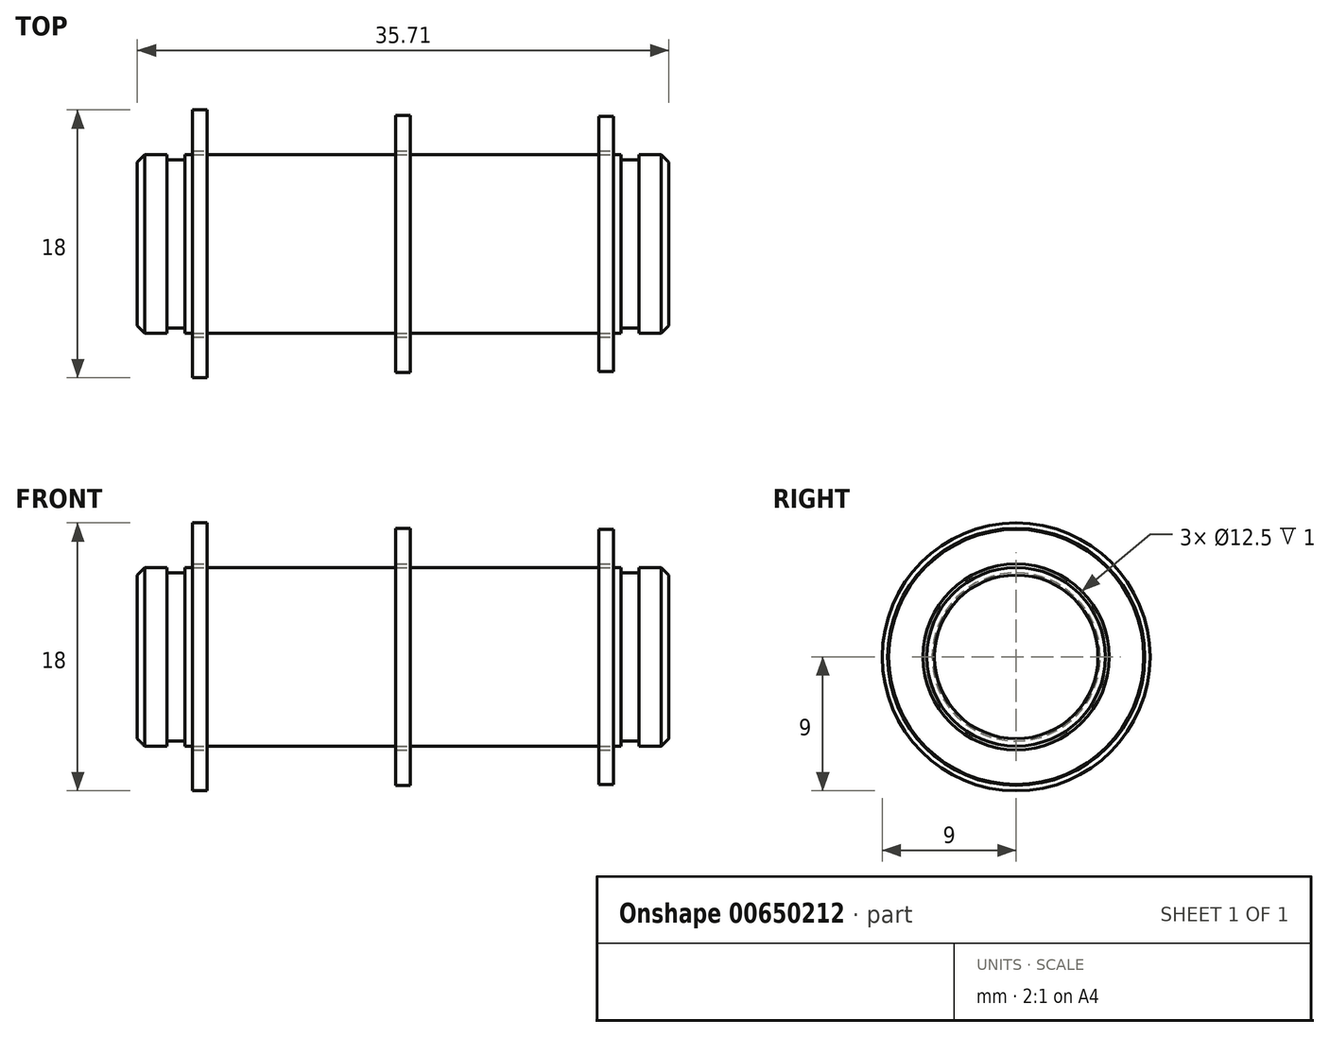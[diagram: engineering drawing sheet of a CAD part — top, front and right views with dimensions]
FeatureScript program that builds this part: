
annotation { "Feature Type Name" : "Feature", "Feature Type Description" : "" }
export const myFeature = defineFeature(function(context is Context, id is Id, definition is map)
    precondition{}
    {
        {
            var Q0;
            Q0=qCreatedBy(makeId("Front.planeOp"),FACE);
            var sketch = newSketch(context, id + "F0", { "sketchPlane" : qUnion([Q0])});
            skLineSegment(sketch, "E0.top", {"start": v(0.5, 6) * mm, "end": v(2, 6) * mm});
            skLineSegment(sketch, "E0.left", {"start": v(0, 0) * mm, "end": v(0, 5.5) * mm});
            skLineSegment(sketch, "E1", {"start": v(2, 6) * mm, "end": v(2, 5.65) * mm});
            skLineSegment(sketch, "E2", {"start": v(2, 5.65) * mm, "end": v(3.2, 5.65) * mm});
            skLineSegment(sketch, "E3", {"start": v(3.2, 5.65) * mm, "end": v(3.2, 6) * mm});
            skLineSegment(sketch, "E4.trimOffspring", {"start": v(3.2, 6) * mm, "end": v(16.7, 6) * mm});
            skLineSegment(sketch, "E5", {"start": v(0.5, 6) * mm, "end": v(0, 5.5) * mm});
            skLineSegment(sketch, "E6.bottom", {"start": v(3.7, 9) * mm, "end": v(4.7, 9) * mm});
            skLineSegment(sketch, "E6.left", {"start": v(3.7, 9) * mm, "end": v(3.7, 6.25) * mm});
            skLineSegment(sketch, "E6.right", {"start": v(4.7, 9) * mm, "end": v(4.7, 6.25) * mm});
            skLineSegment(sketch, "E7", {"start": v(17.35, 6.25) * mm, "end": v(17.35, 8.63) * mm});
            skLineSegment(sketch, "E8", {"start": v(17.85, 8.63) * mm, "end": v(17.35, 8.63) * mm});
            skLineSegment(sketch, "E9.MirrorCS", {"start": v(17.85, 8.63) * mm, "end": v(18.35, 8.63) * mm});
            skLineSegment(sketch, "E10.MirrorCS", {"start": v(32, 8.57) * mm, "end": v(31, 8.57) * mm});
            skLineSegment(sketch, "E11.MirrorCS", {"start": v(32.5, 5.65) * mm, "end": v(32.5, 6) * mm});
            skLineSegment(sketch, "E12.MirrorCS", {"start": v(35.2, 6) * mm, "end": v(35.7, 5.5) * mm});
            skLineSegment(sketch, "E13.MirrorCS", {"start": v(33.7, 6) * mm, "end": v(33.7, 5.65) * mm});
            skLineSegment(sketch, "E14.MirrorCS", {"start": v(32, 8.57) * mm, "end": v(32, 6.25) * mm});
            skLineSegment(sketch, "E15.MirrorCS", {"start": v(31, 8.57) * mm, "end": v(31, 6.25) * mm});
            skLineSegment(sketch, "E16.MirrorCS", {"start": v(17.85, 6.25) * mm, "end": v(17.85, 8.63) * mm});
            skLineSegment(sketch, "E17.MirrorCS", {"start": v(35.2, 6) * mm, "end": v(33.7, 6) * mm});
            skLineSegment(sketch, "E18.MirrorCS", {"start": v(35.7, 0) * mm, "end": v(19, 0) * mm});
            skLineSegment(sketch, "E19.MirrorCS", {"start": v(35.7, 0) * mm, "end": v(35.7, 5.5) * mm});
            skLineSegment(sketch, "E20.MirrorCS", {"start": v(18.35, 6.25) * mm, "end": v(18.35, 8.63) * mm});
            skLineSegment(sketch, "E21.MirrorCS", {"start": v(33.7, 5.65) * mm, "end": v(32.5, 5.65) * mm});
            skLineSegment(sketch, "E22", {"start": v(3.7, 6.25) * mm, "end": v(4.7, 6.25) * mm});
            skPoint(sketch, "E23.orphan", {"position": v(3.7, 6) * mm});
            skLineSegment(sketch, "E24", {"start": v(32, 6.25) * mm, "end": v(31, 6.25) * mm});
            skLineSegment(sketch, "E25", {"start": v(18.35, 6.25) * mm, "end": v(17.35, 6.25) * mm});
            skLineSegment(sketch, "E26", {"start": v(32.5, 6) * mm, "end": v(19, 6) * mm});
            skLineSegment(sketch, "E27", {"start": v(19, 6) * mm, "end": v(16.7, 6) * mm});
            skLineSegment(sketch, "E28", {"start": v(19, 0) * mm, "end": v(0, 0) * mm});
            skSolve(sketch);
        }
        {
            var Q0;
            Q0=makeQuery(id+"F0.imprint","IMPRINT",FACE,{"disambiguationData":[TD([[makeQuery(id+"F0.imprint","IMPRINT",EDGE,{"derivedFrom":sQuery(id+"F0.wireOp",EDGE,"E0.top")}),-1.0]])]});
            var Q1;
            Q1=makeQuery(id+"F0.imprint","IMPRINT",FACE,{"disambiguationData":[TD([[makeQuery(id+"F0.imprint","IMPRINT",EDGE,{"derivedFrom":sQuery(id+"F0.wireOp",EDGE,"E10.MirrorCS")}),1.0]])]});
            var Q2;
            Q2=makeQuery(id+"F0.imprint","IMPRINT",FACE,{"disambiguationData":[TD([[makeQuery(id+"F0.imprint","IMPRINT",EDGE,{"derivedFrom":sQuery(id+"F0.wireOp",EDGE,"E9.MirrorCS")}),-1.0]])]});
            var Q3;
            {var subQ0=sQuery(id+"F0.wireOp",EDGE,"E7");Q3=makeQuery(id+"F0.imprint","IMPRINT",FACE,{"disambiguationData":[TD([[makeQuery(id+"F0.imprint","IMPRINT",EDGE,{"derivedFrom":subQ0}),-1.0]])]});}
            var Q4;
            Q4=makeQuery(id+"F0.imprint","IMPRINT",FACE,{"disambiguationData":[TD([[makeQuery(id+"F0.imprint","IMPRINT",EDGE,{"derivedFrom":sQuery(id+"F0.wireOp",EDGE,"E6.bottom")}),-1.0]])]});
            var Q5;
            Q5=sQuery(id+"F0.wireOp",EDGE,"E28");
            revolve(context, id + "F1", {"entities" : qUnion([Q0, Q1, Q2, Q3, Q4]), "axis" : qUnion([Q5]), "revolveType" : RevolveType.FULL});
        }
    });
